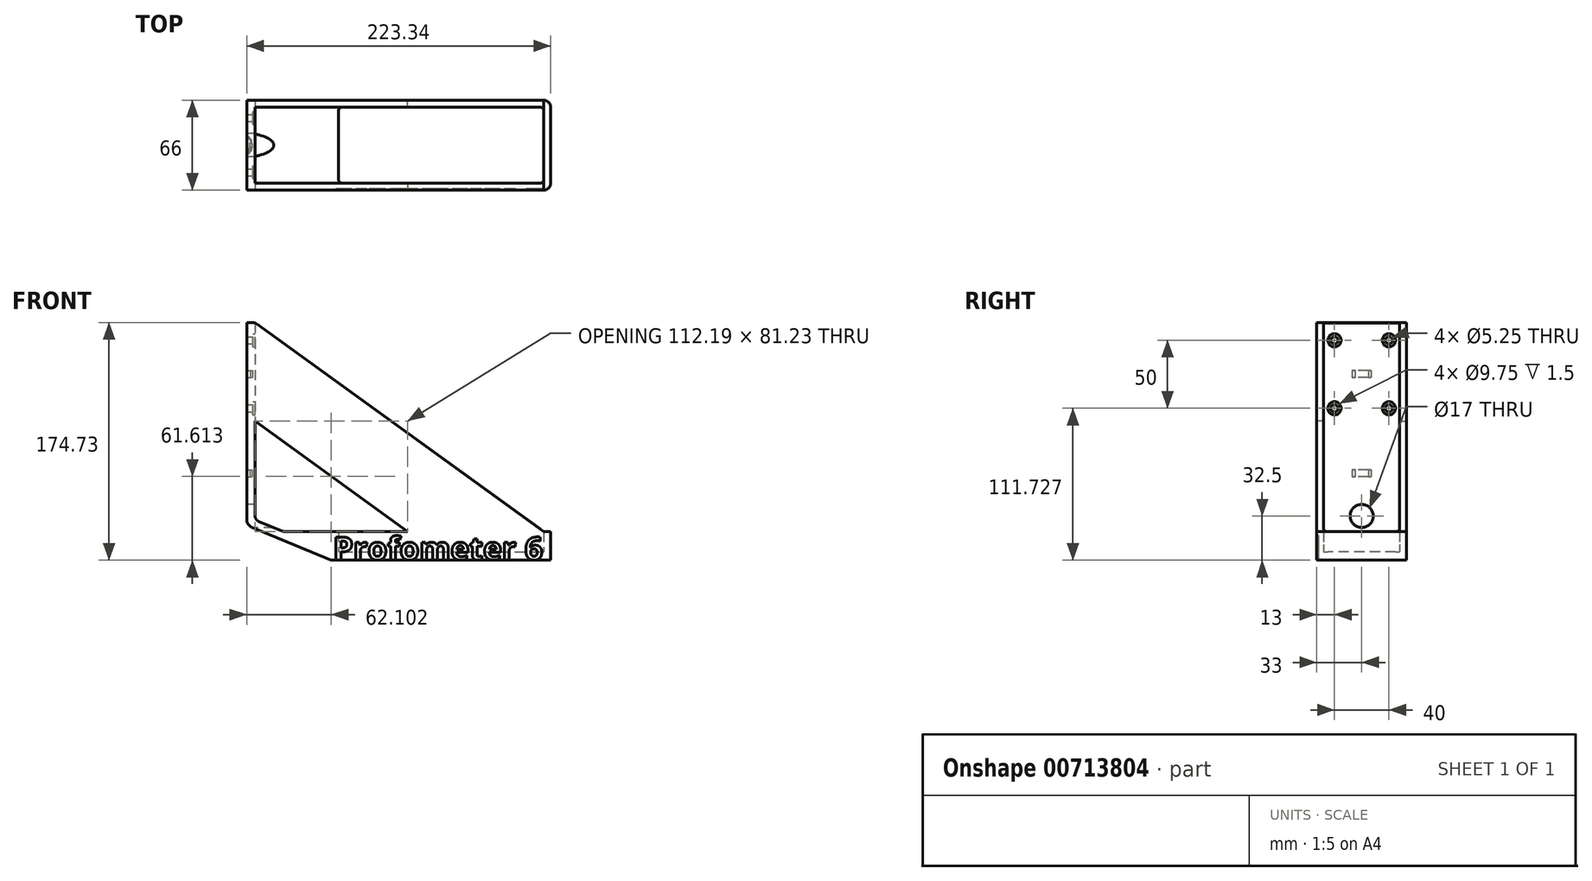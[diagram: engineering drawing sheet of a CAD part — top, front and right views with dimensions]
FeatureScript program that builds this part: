
annotation { "Feature Type Name" : "Feature", "Feature Type Description" : "" }
export const myFeature = defineFeature(function(context is Context, id is Id, definition is map)
    precondition{}
    {
        {
            var Q0;
            Q0=qCreatedBy(makeId("Front.planeOp"),FACE);
            var sketch = newSketch(context, id + "F0", { "sketchPlane" : qUnion([Q0])});
            skLineSegment(sketch, "E0", {"start": v(-63.34, 174.73) * mm, "end": v(-63.34, 29.73) * mm});
            skLineSegment(sketch, "E1", {"start": v(0, 0) * mm, "end": v(160, 0) * mm});
            skLineSegment(sketch, "E2", {"start": v(-63.34, 174.73) * mm, "end": v(-57.34, 174.73) * mm});
            skLineSegment(sketch, "E3", {"start": v(-57.34, 174.73) * mm, "end": v(-57.34, 29.73) * mm});
            skLineSegment(sketch, "E4", {"start": v(-57.34, 29.73) * mm, "end": v(0, 6) * mm});
            skLineSegment(sketch, "E5", {"start": v(0, 6) * mm, "end": v(160, 6) * mm});
            skLineSegment(sketch, "E6", {"start": v(160, 6) * mm, "end": v(160, 0) * mm});
            skLineSegment(sketch, "E7", {"start": v(0, 6) * mm, "end": v(0, 0) * mm, "construction": true});
            skLineSegment(sketch, "E8", {"start": v(-63.34, 29.73) * mm, "end": v(-57.34, 29.73) * mm, "construction": true});
            skLineSegment(sketch, "E9", {"start": v(-63.34, 29.73) * mm, "end": v(-63.34, 25.72) * mm});
            skLineSegment(sketch, "E10", {"start": v(-63.34, 25.72) * mm, "end": v(-1.2, 0) * mm});
            skLineSegment(sketch, "E11", {"start": v(-1.2, 0) * mm, "end": v(0, 0) * mm});
            skLineSegment(sketch, "E12", {"start": v(-57.34, 151.5) * mm, "end": v(-57.34, 174.73) * mm});
            skSolve(sketch);
        }
        {
            var Q0;
            Q0=makeQuery(id+"F0.imprint","IMPRINT",FACE,{"disambiguationData":[TD([[makeQuery(id+"F0.imprint","IMPRINT",EDGE,{"derivedFrom":sQuery(id+"F0.wireOp",EDGE,"E0")}),1.0]])]});
            extrude(context, id + "F1", {"entities" : qUnion([Q0]), "depth" : 66 * mm, "offsetDistance" : 25 * mm});
        }
        {
            var Q0;
            Q0=makeQuery(id+"F1.opExtrude","SWEPT_FACE",FACE,{"disambiguationData":[OSD([sQuery(id+"F0.wireOp",EDGE,"E3")])]});
            var sketch = newSketch(context, id + "F2", { "sketchPlane" : qUnion([Q0])});
            skPoint(sketch, "E13", {"position": v(-53, 161.73) * mm});
            skPoint(sketch, "E14", {"position": v(-13, 161.73) * mm});
            skPoint(sketch, "E15", {"position": v(-53, 111.73) * mm});
            skPoint(sketch, "E16", {"position": v(-13, 111.73) * mm});
            skPoint(sketch, "E17", {"position": v(-33, 32.5) * mm});
            skLineSegment(sketch, "E18", {"start": v(-33, 32.5) * mm, "end": v(-33, 0) * mm, "construction": true});
            skCircle(sketch, "E19", {"center": v(-33, 32.5) * mm, "radius": 8.5 * mm});
            skLineSegment(sketch, "E20", {"start": v(-13, 161.73) * mm, "end": v(-13, 111.73) * mm, "construction": true});
            skLineSegment(sketch, "E21", {"start": v(-53, 111.73) * mm, "end": v(-13, 111.73) * mm, "construction": true});
            skLineSegment(sketch, "E22", {"start": v(-53, 161.73) * mm, "end": v(-53, 111.73) * mm, "construction": true});
            skLineSegment(sketch, "E23", {"start": v(-53, 161.73) * mm, "end": v(-13, 161.73) * mm, "construction": true});
            skLineSegment(sketch, "E24", {"start": v(-13, 161.73) * mm, "end": v(0, 161.73) * mm, "construction": true});
            skLineSegment(sketch, "E25", {"start": v(-53, 161.73) * mm, "end": v(-66, 161.73) * mm, "construction": true});
            skSolve(sketch);
        }
        {
            var Q0;
            Q0=sQuery(id+"F2.wireOp",VERTEX,"E13");
            var Q1;
            Q1=sQuery(id+"F2.wireOp",VERTEX,"E14");
            var Q2;
            Q2=sQuery(id+"F2.wireOp",VERTEX,"E16");
            var Q3;
            Q3=sQuery(id+"F2.wireOp",VERTEX,"E15");
            var Q4;
            Q4=sQuery(id+"F2.wireOp",VERTEX,"d87060a9-d560-4328-90d6-120cbc4be284");
            var Q5;
            Q5=sQuery(id+"F2.wireOp",VERTEX,"b24fa170-ac1a-4f8a-a9ad-690cf26e2aba");
            var Q6;
            Q6=makeQuery(id+"F1.opExtrude","SWEPT_BODY",BODY,{"disambiguationData":[OSD([sQuery(id+"F0.wireOp",EDGE,"E0"),sQuery(id+"F0.wireOp",EDGE,"pjV70WAZ-Rcya-7Rw0-g60Y-Jp7lQ99mjT5H"),sQuery(id+"F0.wireOp",EDGE,"E1"),sQuery(id+"F0.wireOp",EDGE,"E2"),sQuery(id+"F0.wireOp",EDGE,"E3"),sQuery(id+"F0.wireOp",EDGE,"E4"),sQuery(id+"F0.wireOp",EDGE,"E5"),sQuery(id+"F0.wireOp",EDGE,"E6")])]});
            hole(context, id + "F3", {"style" : HoleStyle.C_BORE, "endStyle" : HoleEndStyle.THROUGH, "holeDiameter" : 5.25 * mm, "cBoreDiameter" : 9.75 * mm, "cBoreDepth" : 1.5 * mm, "isTappedThrough" : true, "tappedDepth" : 12 * mm, "tapClearance" : 3, "locations" : qUnion([Q0, Q1, Q2, Q3, Q4, Q5]), "scope" : qUnion([Q6]), "majorDiameter" : 5 * mm});
        }
        {
            var Q0;
            Q0=makeQuery(id+"F1.opExtrude","SWEPT_EDGE",EDGE,{"disambiguationData":[OSD([sQuery(id+"F0.wireOp",EDGE,"E9"),sQuery(id+"F0.wireOp",EDGE,"E10")])]});
            var Q1;
            Q1=makeQuery(id+"F1.opExtrude","SWEPT_EDGE",EDGE,{"disambiguationData":[OSD([sQuery(id+"F0.wireOp",EDGE,"E10"),sQuery(id+"F0.wireOp",EDGE,"E11")])]});
            fillet(context, id + "F4", {"entities" : qUnion([Q0, Q1]), "radius" : 6 * mm, "tangentPropagation" : true, "allowEdgeOverflow" : false});
        }
        {
            var Q0;
            Q0=makeQuery(id+"F1.opExtrude","CAP_EDGE",EDGE,{"disambiguationData":[OSD([sQuery(id+"F0.wireOp",EDGE,"E6")])],"isStart":false});
            var Q1;
            Q1=makeQuery(id+"F1.opExtrude","CAP_EDGE",EDGE,{"disambiguationData":[OSD([sQuery(id+"F0.wireOp",EDGE,"E6")])],"isStart":true});
            fillet(context, id + "F5", {"entities" : qUnion([Q0, Q1]), "radius" : 5 * mm, "tangentPropagation" : true, "allowEdgeOverflow" : false});
        }
        {
            var Q0;
            Q0=makeQuery(id+"F1.opExtrude","SWEPT_FACE",FACE,{"disambiguationData":[OSD([sQuery(id+"F0.wireOp",EDGE,"E5")])]});
            var sketch = newSketch(context, id + "F6", { "sketchPlane" : qUnion([Q0])});
            skLineSegment(sketch, "E26.bottom", {"start": v(4, -5) * mm, "end": v(155, -5) * mm});
            skLineSegment(sketch, "E26.top", {"start": v(4, -61) * mm, "end": v(155, -61) * mm});
            skLineSegment(sketch, "E26.left", {"start": v(4, -5) * mm, "end": v(4, -61) * mm});
            skLineSegment(sketch, "E26.right", {"start": v(155, -5) * mm, "end": v(155, -61) * mm});
            skSolve(sketch);
        }
        {
            var Q0;
            Q0=makeQuery(id+"F6.imprint","IMPRINT",FACE,{"disambiguationData":[TD([[makeQuery(id+"F6.imprint","IMPRINT",EDGE,{"derivedFrom":sQuery(id+"F6.wireOp",EDGE,"E26.bottom")}),1.0]])]});
            var Q1;
            Q1=makeQuery(id+"F1.opExtrude","SWEPT_FACE",FACE,{"disambiguationData":[OSD([sQuery(id+"F0.wireOp",EDGE,"E4")])]});
            extrude(context, id + "F7", {"entities" : qUnion([Q0, Q1]), "operationType" : NewBodyOperationType.ADD, "depth" : 15 * mm, "offsetDistance" : 25 * mm});
        }
        {
            var Q0;
            {var subQ0=sQuery(id+"F0.wireOp",EDGE,"E5");var subQ1=sQuery(id+"F0.wireOp",EDGE,"E4");var subQ2=sQuery(id+"F0.wireOp",EDGE,"E12");var subQ3=sQuery(id+"F0.wireOp",EDGE,"E3");Q0=makeQuery(id+"F7.boolean.opBoolean","MERGE",FACE,{"derivedFrom":[makeQuery(id+"FKc4sbz5m3Xd0Rw_1.boolean.opBoolean","MERGE",FACE,{"derivedFrom":[makeQuery(id+"F1.opExtrude","CAP_FACE",FACE,{"disambiguationData":[OSD([sQuery(id+"F0.wireOp",EDGE,"E0"),sQuery(id+"F0.wireOp",EDGE,"E1"),sQuery(id+"F0.wireOp",EDGE,"E2"),subQ3,subQ1,subQ0,sQuery(id+"F0.wireOp",EDGE,"E6"),sQuery(id+"F0.wireOp",EDGE,"E9"),sQuery(id+"F0.wireOp",EDGE,"E10"),sQuery(id+"F0.wireOp",EDGE,"E11"),subQ2])],"isStart":false}),makeQuery(id+"FKc4sbz5m3Xd0Rw_1.opExtrude","CAP_FACE",FACE,{"disambiguationData":[OSD([subQ3,subQ2,sQuery(id+"Fz0MRBaBYZ9fZvT_1.wireOp",EDGE,"EJlEOmPm-1Df5-yPf7-G4m8-KROSQp18Kuid"),sQuery(id+"Fz0MRBaBYZ9fZvT_1.wireOp",EDGE,"qMokFWCy-sjGW-ftmy-MUSx-eC0m0w4ICkbd")])],"isStart":true})]}),makeQuery(id+"F7.opExtrude","SWEPT_FACE",FACE,{"disambiguationData":[OSD([subQ1]),TDD([makeQuery(id+"F1.opExtrude","CAP_EDGE",EDGE,{"disambiguationData":[OSD([subQ1])],"isStart":false})])]}),makeQuery(id+"F7.opExtrude","SWEPT_FACE",FACE,{"disambiguationData":[OSD([subQ0]),TDD([makeQuery(id+"F6.imprint","IMPRINT",EDGE,{"derivedFrom":makeQuery(id+"F1.opExtrude","CAP_EDGE",EDGE,{"disambiguationData":[OSD([subQ0])],"isStart":false})})])]})]});}
            var sketch = newSketch(context, id + "F8", { "sketchPlane" : qUnion([Q0])});
            skLineSegment(sketch, "E27", {"start": v(0, 21) * mm, "end": v(-36.25, 21) * mm});
            skLineSegment(sketch, "E28", {"start": v(0, 0) * mm, "end": v(0, 6) * mm, "construction": true});
            skLineSegment(sketch, "E29", {"start": v(0, 6) * mm, "end": v(-57.34, 29.73) * mm, "construction": true});
            skLineSegment(sketch, "E30", {"start": v(-57.34, 29.73) * mm, "end": v(-59.63, 24.18) * mm, "construction": true});
            skLineSegment(sketch, "E31", {"start": v(-57.34, 29.73) * mm, "end": v(-63.34, 29.73) * mm, "construction": true});
            skLineSegment(sketch, "E32", {"start": v(-36.25, 21) * mm, "end": v(-57.34, 29.73) * mm});
            skLineSegment(sketch, "E33", {"start": v(-57.34, 44.73) * mm, "end": v(0, 21) * mm});
            skLineSegment(sketch, "E34", {"start": v(-57.34, 44.73) * mm, "end": v(-57.34, 29.73) * mm});
            skSolve(sketch);
        }
        {
            var Q0;
            Q0=makeQuery(id+"F8.imprint","IMPRINT",FACE,{"disambiguationData":[TD([[makeQuery(id+"F8.imprint","IMPRINT",EDGE,{"derivedFrom":sQuery(id+"F8.wireOp",EDGE,"E27")}),-1.0]])]});
            extrude(context, id + "F9", {"entities" : qUnion([Q0]), "operationType" : NewBodyOperationType.REMOVE, "endBound" : BoundingType.THROUGH_ALL, "oppositeDirection" : true, "depth" : 25 * mm, "offsetDistance" : 25 * mm});
        }
        {
            var Q0;
            {var subQ0=sQuery(id+"F0.wireOp",EDGE,"E5");var subQ1=sQuery(id+"F0.wireOp",EDGE,"E4");Q0=makeQuery(id+"F7.boolean.opBoolean","MERGE",FACE,{"derivedFrom":[makeQuery(id+"F1.opExtrude","CAP_FACE",FACE,{"disambiguationData":[OSD([sQuery(id+"F0.wireOp",EDGE,"E0"),sQuery(id+"F0.wireOp",EDGE,"E1"),sQuery(id+"F0.wireOp",EDGE,"E2"),sQuery(id+"F0.wireOp",EDGE,"E3"),subQ1,subQ0,sQuery(id+"F0.wireOp",EDGE,"E6"),sQuery(id+"F0.wireOp",EDGE,"E9"),sQuery(id+"F0.wireOp",EDGE,"E10"),sQuery(id+"F0.wireOp",EDGE,"E11"),sQuery(id+"F0.wireOp",EDGE,"E12")])],"isStart":true}),makeQuery(id+"F7.opExtrude","SWEPT_FACE",FACE,{"disambiguationData":[OSD([subQ1]),TDD([makeQuery(id+"F1.opExtrude","CAP_EDGE",EDGE,{"disambiguationData":[OSD([subQ1])],"isStart":true})])]}),makeQuery(id+"F7.opExtrude","SWEPT_FACE",FACE,{"disambiguationData":[OSD([subQ0]),TDD([makeQuery(id+"F6.imprint","IMPRINT",EDGE,{"derivedFrom":makeQuery(id+"F1.opExtrude","CAP_EDGE",EDGE,{"disambiguationData":[OSD([subQ0])],"isStart":true})})])]})]});}
            var sketch = newSketch(context, id + "F10", { "sketchPlane" : qUnion([Q0])});
            skLineSegment(sketch, "E35", {"start": v(57.34, 174.73) * mm, "end": v(-155, 21) * mm});
            skLineSegment(sketch, "E36", {"start": v(57.34, 102.23) * mm, "end": v(-54.86, 21) * mm});
            skLineSegment(sketch, "E37", {"start": v(-155, 21) * mm, "end": v(-54.86, 21) * mm});
            skSolve(sketch);
        }
        {
            var Q0;
            {var subQ0=sQuery(id+"F10.wireOp",EDGE,"E35");Q0=makeQuery(id+"F10.imprint","IMPRINT",FACE,{"disambiguationData":[TD([[makeQuery(id+"F10.imprint","IMPRINT",EDGE,{"derivedFrom":subQ0}),1.0]])]});}
            extrude(context, id + "F11", {"entities" : qUnion([Q0]), "operationType" : NewBodyOperationType.ADD, "oppositeDirection" : true, "depth" : 5 * mm, "offsetDistance" : 25 * mm});
        }
        {
            var Q0;
            {var subQ0=sQuery(id+"F0.wireOp",EDGE,"E5");var subQ1=sQuery(id+"F0.wireOp",EDGE,"E4");Q0=makeQuery(id+"F7.boolean.opBoolean","MERGE",FACE,{"derivedFrom":[makeQuery(id+"F1.opExtrude","CAP_FACE",FACE,{"disambiguationData":[OSD([sQuery(id+"F0.wireOp",EDGE,"E0"),sQuery(id+"F0.wireOp",EDGE,"E1"),sQuery(id+"F0.wireOp",EDGE,"E2"),sQuery(id+"F0.wireOp",EDGE,"E3"),subQ1,subQ0,sQuery(id+"F0.wireOp",EDGE,"E6"),sQuery(id+"F0.wireOp",EDGE,"E9"),sQuery(id+"F0.wireOp",EDGE,"E10"),sQuery(id+"F0.wireOp",EDGE,"E11"),sQuery(id+"F0.wireOp",EDGE,"E12")])],"isStart":false}),makeQuery(id+"F7.opExtrude","SWEPT_FACE",FACE,{"disambiguationData":[OSD([subQ1]),TDD([makeQuery(id+"F1.opExtrude","CAP_EDGE",EDGE,{"disambiguationData":[OSD([subQ1])],"isStart":false})])]}),makeQuery(id+"F7.opExtrude","SWEPT_FACE",FACE,{"disambiguationData":[OSD([subQ0]),TDD([makeQuery(id+"F6.imprint","IMPRINT",EDGE,{"derivedFrom":makeQuery(id+"F1.opExtrude","CAP_EDGE",EDGE,{"disambiguationData":[OSD([subQ0])],"isStart":false})})])]})]});}
            var sketch = newSketch(context, id + "F12", { "sketchPlane" : qUnion([Q0])});
            skLineSegment(sketch, "E38", {"start": v(-57.34, 174.73) * mm, "end": v(155, 21) * mm});
            skLineSegment(sketch, "E39", {"start": v(-57.33, 102.23) * mm, "end": v(54.86, 21) * mm});
            skLineSegment(sketch, "E40", {"start": v(54.86, 21) * mm, "end": v(155, 21) * mm});
            skLineSegment(sketch, "E41", {"start": v(-57.34, 102.23) * mm, "end": v(-57.34, 174.73) * mm});
            skSolve(sketch);
        }
        {
            var Q0;
            Q0=makeQuery(id+"F12.imprint","IMPRINT",FACE,{"disambiguationData":[TD([[makeQuery(id+"F12.imprint","IMPRINT",EDGE,{"derivedFrom":sQuery(id+"F12.wireOp",EDGE,"E38")}),-1.0]])]});
            extrude(context, id + "F13", {"entities" : qUnion([Q0]), "operationType" : NewBodyOperationType.ADD, "oppositeDirection" : true, "depth" : 5 * mm, "offsetDistance" : 25 * mm});
        }
        {
            var Q0;
            Q0=makeQuery(id+"F9.boolean.opBoolean","COPY",EDGE,{"derivedFrom":makeQuery(id+"F9.opExtrude","SWEPT_EDGE",EDGE,{"disambiguationData":[OSD([sQuery(id+"F8.wireOp",EDGE,"E32"),sQuery(id+"F8.wireOp",EDGE,"E34")])]})});
            var Q1;
            Q1=makeQuery(id+"F9.boolean.opBoolean","COPY",EDGE,{"derivedFrom":makeQuery(id+"F9.opExtrude","SWEPT_EDGE",EDGE,{"disambiguationData":[OSD([sQuery(id+"F8.wireOp",EDGE,"E27"),sQuery(id+"F8.wireOp",EDGE,"E32")])]})});
            fillet(context, id + "F14", {"entities" : qUnion([Q0, Q1]), "radius" : 5 * mm, "allowEdgeOverflow" : false});
        }
        {
            var Q0;
            {var subQ0=sQuery(id+"F0.wireOp",EDGE,"E2");Q0=makeQuery(id+"F13.boolean.opBoolean","MERGE",EDGE,{"derivedFrom":[makeQuery(id+"F11.boolean.opBoolean","SPLIT",EDGE,{"derivedFrom":makeQuery(id+"F1.opExtrude","SWEPT_EDGE",EDGE,{"disambiguationData":[OSD([subQ0,sQuery(id+"F0.wireOp",EDGE,"E12")])]})}),makeQuery(id+"F13.opExtrude","SWEPT_EDGE",EDGE,{"disambiguationData":[OSD([subQ0,sQuery(id+"F12.wireOp",EDGE,"E38"),sQuery(id+"F12.wireOp",EDGE,"E41")])]})]});}
            var Q1;
            {var subQ0=sQuery(id+"F0.wireOp",EDGE,"E12");var subQ1=sQuery(id+"F0.wireOp",EDGE,"E2");Q1=makeQuery(id+"F11.boolean.opBoolean","MERGE",EDGE,{"derivedFrom":[makeQuery(id+"F1.opExtrude","SWEPT_EDGE",EDGE,{"disambiguationData":[OSD([subQ1,subQ0])]}),makeQuery(id+"F11.opExtrude","SWEPT_EDGE",EDGE,{"disambiguationData":[OSD([sQuery(id+"F0.wireOp",EDGE,"E0"),sQuery(id+"F0.wireOp",EDGE,"E1"),subQ1,sQuery(id+"F0.wireOp",EDGE,"E3"),sQuery(id+"F0.wireOp",EDGE,"E4"),sQuery(id+"F0.wireOp",EDGE,"E5"),sQuery(id+"F0.wireOp",EDGE,"E6"),sQuery(id+"F0.wireOp",EDGE,"E9"),sQuery(id+"F0.wireOp",EDGE,"E10"),sQuery(id+"F0.wireOp",EDGE,"E11"),subQ0,sQuery(id+"F8.wireOp",EDGE,"E34"),sQuery(id+"F10.wireOp",EDGE,"E35")])]})]});}
            fillet(context, id + "F15", {"entities" : qUnion([Q0, Q1]), "radius" : 5 * mm, "allowEdgeOverflow" : false});
        }
        {
            var Q0;
            Q0=makeQuery(id+"F7.opExtrude","SWEPT_EDGE",EDGE,{"disambiguationData":[OSD([sQuery(id+"F6.wireOp",EDGE,"E26.top"),sQuery(id+"F6.wireOp",EDGE,"E26.left")])]});
            var Q1;
            Q1=makeQuery(id+"F7.opExtrude","SWEPT_EDGE",EDGE,{"disambiguationData":[OSD([sQuery(id+"F6.wireOp",EDGE,"E26.bottom"),sQuery(id+"F6.wireOp",EDGE,"E26.left")])]});
            var Q2;
            Q2=makeQuery(id+"F7.opExtrude","SWEPT_EDGE",EDGE,{"disambiguationData":[OSD([sQuery(id+"F6.wireOp",EDGE,"E26.bottom"),sQuery(id+"F6.wireOp",EDGE,"E26.right")])]});
            var Q3;
            Q3=makeQuery(id+"F7.opExtrude","SWEPT_EDGE",EDGE,{"disambiguationData":[OSD([sQuery(id+"F6.wireOp",EDGE,"E26.top"),sQuery(id+"F6.wireOp",EDGE,"E26.right")])]});
            fillet(context, id + "F16", {"entities" : qUnion([Q0, Q1, Q2, Q3]), "radius" : 3 * mm, "tangentPropagation" : true, "allowEdgeOverflow" : false});
        }
        {
            var Q0;
            {var subQ0=sQuery(id+"F2.wireOp",EDGE,"E19");var subQ1=makeQuery(id+"F1.opExtrude","SWEPT_EDGE",EDGE,{"disambiguationData":[OSD([sQuery(id+"F0.wireOp",EDGE,"E3"),sQuery(id+"F0.wireOp",EDGE,"E4")])]});var subQ2=makeQuery(id+"F2.imprint","INTERSECT",VERTEX,{"disambiguationData":[OD(0.0)],"derivedFrom":[subQ1,subQ0]});Q0=makeQuery(id+"F2.imprint","IMPRINT",FACE,{"disambiguationData":[TD([[makeQuery(id+"F2.imprint","IMPRINT",EDGE,{"disambiguationData":[TD([[subQ2,1.0]])],"derivedFrom":subQ0}),1.0]])]});}
            var Q1;
            {var subQ0=sQuery(id+"F2.wireOp",EDGE,"E19");var subQ1=makeQuery(id+"F1.opExtrude","SWEPT_EDGE",EDGE,{"disambiguationData":[OSD([sQuery(id+"F0.wireOp",EDGE,"E3"),sQuery(id+"F0.wireOp",EDGE,"E4")])]});var subQ2=makeQuery(id+"F2.imprint","INTERSECT",VERTEX,{"disambiguationData":[OD(0.0)],"derivedFrom":[subQ1,subQ0]});Q1=makeQuery(id+"F2.imprint","IMPRINT",FACE,{"disambiguationData":[TD([[makeQuery(id+"F2.imprint","IMPRINT",EDGE,{"disambiguationData":[TD([[subQ2,-1.0]])],"derivedFrom":subQ0}),1.0]])]});}
            var Q2;
            Q2=sQuery(id+"F2.wireOp",EDGE,"E19");
            extrude(context, id + "F17", {"entities" : qUnion([Q0, Q1]), "operationType" : NewBodyOperationType.REMOVE, "surfaceEntities" : qUnion([Q2]), "endBound" : BoundingType.SYMMETRIC, "depth" : 130 * mm, "offsetDistance" : 25 * mm});
        }
        {
            var Q0;
            Q0=makeQuery(id+"F1.opExtrude","SWEPT_FACE",FACE,{"disambiguationData":[OSD([sQuery(id+"F0.wireOp",EDGE,"E0"),sQuery(id+"F0.wireOp",EDGE,"E9")])]});
            var sketch = newSketch(context, id + "F18", { "sketchPlane" : qUnion([Q0])});
            skLineSegment(sketch, "E42", {"start": v(0, 64.03) * mm, "end": v(66, 64.03) * mm, "construction": true});
            skSolve(sketch);
        }
        {
            var Q0;
            Q0=sQuery(id+"F18.wireOp",EDGE,"E42");
            cPlane(context, id + "F19", {"entities" : qUnion([Q0]), "cplaneType" : CPlaneType.LINE_ANGLE, "offset" : 25 * mm, "angle" : 0 * degree, "oppositeDirection" : true, "width" : 150 * mm, "height" : 150 * mm});
        }
        {
            var Q0;
            Q0=qCreatedBy(id+"F19.planeOp",FACE);
            var sketch = newSketch(context, id + "F20", { "sketchPlane" : qUnion([Q0])});
            skArc(sketch, "E43", {"start": v(-63.34, 26) * mm, "mid": v(-59.34, 33) * mm, "end": v(-63.34, 40) * mm});
            skLineSegment(sketch, "E44", {"start": v(-63.34, 26) * mm, "end": v(-63.34, 0) * mm, "construction": true});
            skLineSegment(sketch, "E45", {"start": v(-63.34, 40) * mm, "end": v(-63.34, 66) * mm, "construction": true});
            skArc(sketch, "E46", {"start": v(-63.34, 28) * mm, "mid": v(-60.98, 33) * mm, "end": v(-63.34, 38) * mm});
            skLineSegment(sketch, "E47", {"start": v(-63.34, 26) * mm, "end": v(-65.1, 26) * mm});
            skLineSegment(sketch, "E48", {"start": v(-63.34, 28) * mm, "end": v(-65.1, 28) * mm});
            skLineSegment(sketch, "E49", {"start": v(-65.1, 26) * mm, "end": v(-65.1, 28) * mm});
            skLineSegment(sketch, "E50", {"start": v(-63.34, 38) * mm, "end": v(-65.04, 38) * mm});
            skLineSegment(sketch, "E51", {"start": v(-63.34, 40) * mm, "end": v(-65.04, 40) * mm});
            skLineSegment(sketch, "E52", {"start": v(-65.04, 38) * mm, "end": v(-65.04, 40) * mm});
            skSolve(sketch);
        }
        {
            var Q0;
            Q0=makeQuery(id+"F20.imprint","IMPRINT",FACE,{"disambiguationData":[TD([[makeQuery(id+"F20.imprint","IMPRINT",EDGE,{"derivedFrom":sQuery(id+"F20.wireOp",EDGE,"E43")}),1.0]])]});
            extrude(context, id + "F21", {"entities" : qUnion([Q0]), "operationType" : NewBodyOperationType.REMOVE, "endBound" : BoundingType.SYMMETRIC, "oppositeDirection" : true, "depth" : 5 * mm, "offsetDistance" : 25 * mm});
        }
        {
            var Q0;
            Q0=qCreatedBy(id+"F19.planeOp",FACE);
            cPlane(context, id + "F22", {"entities" : qUnion([Q0]), "cplaneType" : CPlaneType.OFFSET, "offset" : 73 * mm, "oppositeDirection" : true, "width" : 150 * mm, "height" : 150 * mm});
        }
        {
            var Q0;
            Q0=qCreatedBy(id+"F22.planeOp",FACE);
            var sketch = newSketch(context, id + "F23", { "sketchPlane" : qUnion([Q0])});
            skArc(sketch, "E53", {"start": v(-63.06, 26) * mm, "mid": v(-59.06, 33) * mm, "end": v(-63.06, 40) * mm});
            skLineSegment(sketch, "E54", {"start": v(-63.06, 26) * mm, "end": v(-63.06, 0) * mm, "construction": true});
            skLineSegment(sketch, "E55", {"start": v(-63.06, 40) * mm, "end": v(-63.06, 66) * mm, "construction": true});
            skArc(sketch, "E56", {"start": v(-63.06, 28) * mm, "mid": v(-60.7, 33) * mm, "end": v(-63.06, 38) * mm});
            skLineSegment(sketch, "E57", {"start": v(-63.06, 26) * mm, "end": v(-64.83, 26) * mm});
            skLineSegment(sketch, "E58", {"start": v(-63.06, 28) * mm, "end": v(-64.83, 28) * mm});
            skLineSegment(sketch, "E59", {"start": v(-64.83, 26) * mm, "end": v(-64.83, 28) * mm});
            skLineSegment(sketch, "E60", {"start": v(-63.06, 38) * mm, "end": v(-64.76, 38) * mm});
            skLineSegment(sketch, "E61", {"start": v(-63.06, 40) * mm, "end": v(-64.76, 40) * mm});
            skLineSegment(sketch, "E62", {"start": v(-64.76, 38) * mm, "end": v(-64.76, 40) * mm});
            skSolve(sketch);
        }
        {
            var Q0;
            Q0=makeQuery(id+"F23.imprint","IMPRINT",FACE,{"disambiguationData":[TD([[makeQuery(id+"F23.imprint","IMPRINT",EDGE,{"derivedFrom":sQuery(id+"F23.wireOp",EDGE,"E53")}),1.0]])]});
            extrude(context, id + "F24", {"entities" : qUnion([Q0]), "operationType" : NewBodyOperationType.REMOVE, "endBound" : BoundingType.SYMMETRIC, "oppositeDirection" : true, "depth" : 5 * mm, "offsetDistance" : 25 * mm});
        }
        {
            var Q0;
            {var subQ0=sQuery(id+"F0.wireOp",EDGE,"E5");var subQ1=sQuery(id+"F0.wireOp",EDGE,"E4");Q0=makeQuery(id+"F13.boolean.opBoolean","MERGE",FACE,{"derivedFrom":[makeQuery(id+"F7.boolean.opBoolean","MERGE",FACE,{"derivedFrom":[makeQuery(id+"F1.opExtrude","CAP_FACE",FACE,{"disambiguationData":[OSD([sQuery(id+"F0.wireOp",EDGE,"E0"),sQuery(id+"F0.wireOp",EDGE,"E1"),sQuery(id+"F0.wireOp",EDGE,"E2"),sQuery(id+"F0.wireOp",EDGE,"E3"),subQ1,subQ0,sQuery(id+"F0.wireOp",EDGE,"E6"),sQuery(id+"F0.wireOp",EDGE,"E9"),sQuery(id+"F0.wireOp",EDGE,"E10"),sQuery(id+"F0.wireOp",EDGE,"E11"),sQuery(id+"F0.wireOp",EDGE,"E12")])],"isStart":false}),makeQuery(id+"F7.opExtrude","SWEPT_FACE",FACE,{"disambiguationData":[OSD([subQ1]),TDD([makeQuery(id+"F1.opExtrude","CAP_EDGE",EDGE,{"disambiguationData":[OSD([subQ1])],"isStart":false})])]}),makeQuery(id+"F7.opExtrude","SWEPT_FACE",FACE,{"disambiguationData":[OSD([subQ0]),TDD([makeQuery(id+"F6.imprint","IMPRINT",EDGE,{"derivedFrom":makeQuery(id+"F1.opExtrude","CAP_EDGE",EDGE,{"disambiguationData":[OSD([subQ0])],"isStart":false})})])]})]}),makeQuery(id+"F13.opExtrude","CAP_FACE",FACE,{"disambiguationData":[OSD([sQuery(id+"F12.wireOp",EDGE,"E38"),sQuery(id+"F12.wireOp",EDGE,"E39"),sQuery(id+"F12.wireOp",EDGE,"E40"),sQuery(id+"F12.wireOp",EDGE,"E41")])],"isStart":true})]});}
            var sketch = newSketch(context, id + "F25", { "sketchPlane" : qUnion([Q0])});
            skText(sketch, "E63", { "text": "Profometer 6", "fontName": "OpenSans-Bold.ttf"});
            const initialGuessF25  = {"E63": [0.00018, 0.00025, 1, 0, 0.01683]};
            skSetInitialGuess(sketch, initialGuessF25);
            skSolve(sketch);
        }
        {
            var Q0;
            Q0=makeQuery(id+"F25.imprint","IMPRINT",FACE,{"disambiguationData":[TD([[makeQuery(id+"F25.imprint","IMPRINT",EDGE,{"derivedFrom":sQuery(id+"F25.wireOp",EDGE,"E63.sketch_text.stroke-0")}),-1.0]])]});
            var Q1;
            Q1=makeQuery(id+"F25.imprint","IMPRINT",FACE,{"disambiguationData":[TD([[makeQuery(id+"F25.imprint","IMPRINT",EDGE,{"derivedFrom":sQuery(id+"F25.wireOp",EDGE,"E63.sketch_text.stroke-16")}),-1.0]])]});
            var Q2;
            Q2=makeQuery(id+"F25.imprint","IMPRINT",FACE,{"disambiguationData":[TD([[makeQuery(id+"F25.imprint","IMPRINT",EDGE,{"derivedFrom":sQuery(id+"F25.wireOp",EDGE,"E63.sketch_text.stroke-29")}),-1.0]])]});
            var Q3;
            Q3=makeQuery(id+"F25.imprint","IMPRINT",FACE,{"disambiguationData":[TD([[makeQuery(id+"F25.imprint","IMPRINT",EDGE,{"derivedFrom":sQuery(id+"F25.wireOp",EDGE,"E63.sketch_text.stroke-47")}),-1.0]])]});
            var Q4;
            Q4=makeQuery(id+"F25.imprint","IMPRINT",FACE,{"disambiguationData":[TD([[makeQuery(id+"F25.imprint","IMPRINT",EDGE,{"derivedFrom":sQuery(id+"F25.wireOp",EDGE,"E63.sketch_text.stroke-65")}),-1.0]])]});
            var Q5;
            Q5=makeQuery(id+"F25.imprint","IMPRINT",FACE,{"disambiguationData":[TD([[makeQuery(id+"F25.imprint","IMPRINT",EDGE,{"derivedFrom":sQuery(id+"F25.wireOp",EDGE,"E63.sketch_text.stroke-83")}),-1.0]])]});
            var Q6;
            Q6=makeQuery(id+"F25.imprint","IMPRINT",FACE,{"disambiguationData":[TD([[makeQuery(id+"F25.imprint","IMPRINT",EDGE,{"derivedFrom":sQuery(id+"F25.wireOp",EDGE,"E63.sketch_text.stroke-111")}),-1.0]])]});
            var Q7;
            Q7=makeQuery(id+"F25.imprint","IMPRINT",FACE,{"disambiguationData":[TD([[makeQuery(id+"F25.imprint","IMPRINT",EDGE,{"derivedFrom":sQuery(id+"F25.wireOp",EDGE,"E63.sketch_text.stroke-131")}),-1.0]])]});
            var Q8;
            Q8=makeQuery(id+"F25.imprint","IMPRINT",FACE,{"disambiguationData":[TD([[makeQuery(id+"F25.imprint","IMPRINT",EDGE,{"derivedFrom":sQuery(id+"F25.wireOp",EDGE,"E63.sketch_text.stroke-149")}),-1.0]])]});
            var Q9;
            Q9=makeQuery(id+"F25.imprint","IMPRINT",FACE,{"disambiguationData":[TD([[makeQuery(id+"F25.imprint","IMPRINT",EDGE,{"derivedFrom":sQuery(id+"F25.wireOp",EDGE,"E63.sketch_text.stroke-169")}),-1.0]])]});
            var Q10;
            Q10=makeQuery(id+"F25.imprint","IMPRINT",FACE,{"disambiguationData":[TD([[makeQuery(id+"F25.imprint","IMPRINT",EDGE,{"derivedFrom":sQuery(id+"F25.wireOp",EDGE,"E63.sketch_text.stroke-182")}),-1.0]])]});
            extrude(context, id + "F26", {"entities" : qUnion([Q0, Q1, Q2, Q3, Q4, Q5, Q6, Q7, Q8, Q9, Q10]), "operationType" : NewBodyOperationType.REMOVE, "oppositeDirection" : true, "depth" : 1 * mm, "offsetDistance" : 25 * mm});
        }
    });
